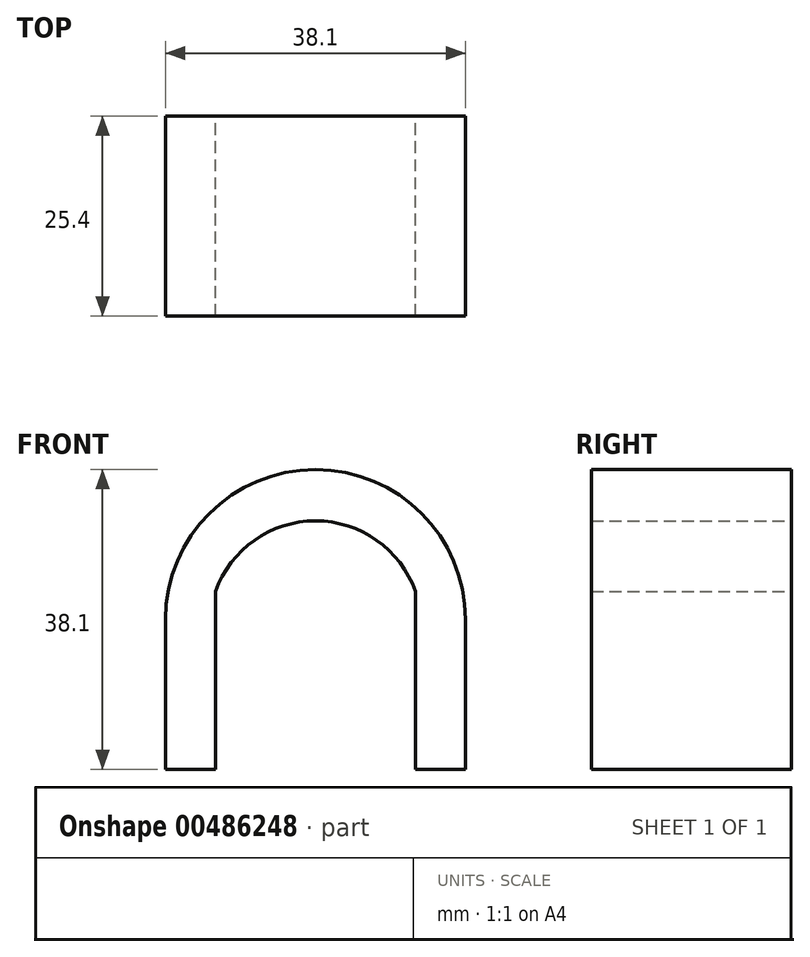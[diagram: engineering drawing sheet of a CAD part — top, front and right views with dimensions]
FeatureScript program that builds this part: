
annotation { "Feature Type Name" : "Feature", "Feature Type Description" : "" }
export const myFeature = defineFeature(function(context is Context, id is Id, definition is map)
    precondition{}
    {
        {
            var Q0;
            Q0=qCreatedBy(makeId("Front.planeOp"),FACE);
            var sketch = newSketch(context, id + "F0", { "sketchPlane" : qUnion([Q0])});
            skLineSegment(sketch, "E0", {"start": v(-4.72, 0) * mm, "end": v(-4.72, 0) * mm});
            skLineSegment(sketch, "E1", {"start": v(-23.77, -19.05) * mm, "end": v(-23.77, -38.1) * mm});
            skLineSegment(sketch, "E2", {"start": v(-23.77, -38.1) * mm, "end": v(-17.42, -38.1) * mm});
            skLineSegment(sketch, "E3", {"start": v(-17.42, -6.35) * mm, "end": v(-17.42, -38.1) * mm});
            skLineSegment(sketch, "E4", {"start": v(14.33, -19.05) * mm, "end": v(14.33, -38.1) * mm});
            skLineSegment(sketch, "E5", {"start": v(14.33, -38.1) * mm, "end": v(7.98, -38.1) * mm});
            skLineSegment(sketch, "E6", {"start": v(7.98, -38.1) * mm, "end": v(7.98, -6.35) * mm});
            skLineSegment(sketch, "E7", {"start": v(7.98, -6.35) * mm, "end": v(-17.42, -6.35) * mm});
            skPoint(sketch, "E8.visualSharp", {"position": v(-23.77, 0) * mm});
            skArc(sketch, "E8.filletArc", {"start": v(-4.72, 0) * mm, "mid": v(-18.2, -5.58) * mm, "end": v(-23.77, -19.05) * mm});
            skPoint(sketch, "E9.visualSharp", {"position": v(14.33, 0) * mm});
            skArc(sketch, "E9.filletArc", {"start": v(14.33, -19.05) * mm, "mid": v(8.75, -5.58) * mm, "end": v(-4.72, 0) * mm});
            skArc(sketch, "E10", {"start": v(7.98, -24.5) * mm, "mid": v(-4.72, -6.52) * mm, "end": v(-17.42, -24.5) * mm});
            skSolve(sketch);
        }
        {
            var Q0;
            Q0=makeQuery(id+"F0.imprint","IMPRINT",FACE,{"disambiguationData":[TD([[makeQuery(id+"F0.imprint","IMPRINT",EDGE,{"derivedFrom":sQuery(id+"F0.wireOp",EDGE,"E1")}),1.0]])]});
            extrude(context, id + "F1", {"entities" : qUnion([Q0]), "depth" : 25.4 * mm});
        }
        {
            var Q0;
            Q0 = qSketchRegion(id + "F0", true);
            extrude(context, id + "F2", {"entities" : qUnion([Q0]), "operationType" : NewBodyOperationType.ADD, "depth" : 25.4 * mm});
        }
        {
            var Q0;
            Q0 = qSketchRegion(id + "F0", true);
            extrude(context, id + "F3", {"entities" : qUnion([Q0]), "operationType" : NewBodyOperationType.ADD, "depth" : 25.4 * mm});
        }
    });
